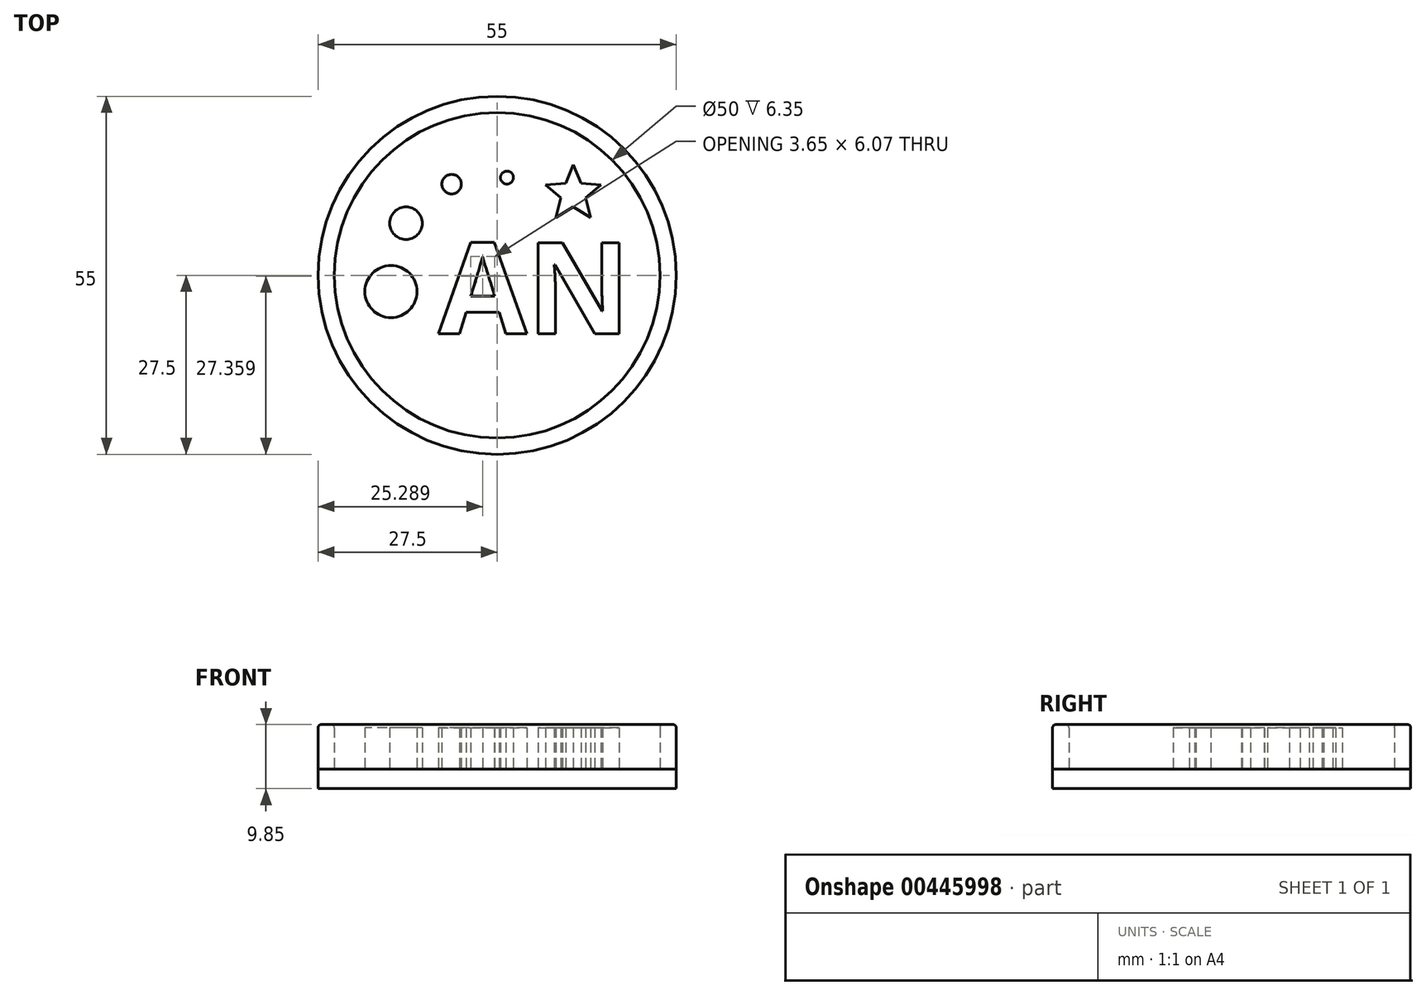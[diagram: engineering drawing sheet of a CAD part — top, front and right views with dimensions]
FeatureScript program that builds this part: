
annotation { "Feature Type Name" : "Feature", "Feature Type Description" : "" }
export const myFeature = defineFeature(function(context is Context, id is Id, definition is map)
    precondition{}
    {
        {
            var Q0;
            Q0=qCreatedBy(makeId("Top.planeOp"),FACE);
            var sketch = newSketch(context, id + "F0", { "sketchPlane" : qUnion([Q0])});
            skCircle(sketch, "E0", {"center": v(0, 0) * mm, "radius": 27.5 * mm});
            skText(sketch, "E1", { "text": "AN", "fontName": "OpenSans-Bold.ttf"});
            skPoint(sketch, "E2", {"position": v(-16.3, -2.5) * mm});
            skPoint(sketch, "E3.1.0", {"position": v(-14, 8) * mm});
            skPoint(sketch, "E3.2.0", {"position": v(-7, 14) * mm});
            skPoint(sketch, "E3.3.0", {"position": v(1.5, 15) * mm});
            skCircle(sketch, "E4", {"center": v(-16.3, -2.5) * mm, "radius": 4 * mm});
            skCircle(sketch, "E5", {"center": v(-14, 8) * mm, "radius": 2.5 * mm});
            skCircle(sketch, "E6", {"center": v(-7, 14) * mm, "radius": 1.5 * mm});
            skPoint(sketch, "E7", {"position": v(11.69, 17) * mm});
            skPoint(sketch, "E8.1.0", {"position": v(7.4, 13.9) * mm});
            skPoint(sketch, "E8.2.0", {"position": v(9.04, 8.86) * mm});
            skPoint(sketch, "E8.3.0", {"position": v(14.33, 8.86) * mm});
            skPoint(sketch, "E8.4.0", {"position": v(15.96, 13.9) * mm});
            skPoint(sketch, "E8.center", {"position": v(11.69, 12.5) * mm});
            skPoint(sketch, "E9", {"position": v(11.69, 10.5) * mm});
            skPoint(sketch, "E10.1.0", {"position": v(13.59, 11.88) * mm});
            skPoint(sketch, "E10.2.0", {"position": v(12.86, 14.12) * mm});
            skPoint(sketch, "E10.3.0", {"position": v(10.5, 14.12) * mm});
            skPoint(sketch, "E10.4.0", {"position": v(9.78, 11.88) * mm});
            skLineSegment(sketch, "E11", {"start": v(11.69, 17) * mm, "end": v(10.5, 14.12) * mm});
            skLineSegment(sketch, "E12", {"start": v(10.5, 14.12) * mm, "end": v(7.4, 13.9) * mm});
            skLineSegment(sketch, "E13", {"start": v(7.4, 13.9) * mm, "end": v(9.78, 11.88) * mm});
            skLineSegment(sketch, "E14", {"start": v(9.78, 11.88) * mm, "end": v(9.04, 8.86) * mm});
            skLineSegment(sketch, "E15", {"start": v(9.04, 8.86) * mm, "end": v(11.69, 10.5) * mm});
            skLineSegment(sketch, "E16", {"start": v(11.69, 10.5) * mm, "end": v(14.33, 8.86) * mm});
            skLineSegment(sketch, "E17", {"start": v(14.33, 8.86) * mm, "end": v(13.59, 11.88) * mm});
            skLineSegment(sketch, "E18", {"start": v(13.59, 11.88) * mm, "end": v(15.96, 13.9) * mm});
            skLineSegment(sketch, "E19", {"start": v(15.96, 13.9) * mm, "end": v(12.86, 14.12) * mm});
            skLineSegment(sketch, "E20", {"start": v(12.86, 14.12) * mm, "end": v(11.69, 17) * mm});
            skCircle(sketch, "E21", {"center": v(1.5, 15) * mm, "radius": 1 * mm});
            skPoint(sketch, "E22", {"position": v(5.5, -1.94) * mm});
            skCircle(sketch, "E23", {"center": v(0, 0) * mm, "radius": 25 * mm});
            const initialGuessF0  = {"E1": [-0.009, -0.009, 1, 0, 0.01413]};
            skSetInitialGuess(sketch, initialGuessF0);
            skSolve(sketch);
        }
        {
            var Q0;
            Q0=makeQuery(id+"F0.imprint","IMPRINT",FACE,{"disambiguationData":[TD([[makeQuery(id+"F0.imprint","IMPRINT",EDGE,{"derivedFrom":sQuery(id+"F0.wireOp",EDGE,"E0")}),1.0]])]});
            var Q1;
            Q1=makeQuery(id+"F0.imprint","IMPRINT",FACE,{"disambiguationData":[TD([[makeQuery(id+"F0.imprint","IMPRINT",EDGE,{"derivedFrom":sQuery(id+"F0.wireOp",EDGE,"E4")}),1.0]])]});
            var Q2;
            Q2=makeQuery(id+"F0.imprint","IMPRINT",FACE,{"disambiguationData":[TD([[makeQuery(id+"F0.imprint","IMPRINT",EDGE,{"derivedFrom":sQuery(id+"F0.wireOp",EDGE,"E5")}),1.0]])]});
            var Q3;
            Q3=makeQuery(id+"F0.imprint","IMPRINT",FACE,{"disambiguationData":[TD([[makeQuery(id+"F0.imprint","IMPRINT",EDGE,{"derivedFrom":sQuery(id+"F0.wireOp",EDGE,"E1.sketch_text.stroke-0")}),-1.0]])]});
            var Q4;
            Q4=makeQuery(id+"F0.imprint","IMPRINT",FACE,{"disambiguationData":[TD([[makeQuery(id+"F0.imprint","IMPRINT",EDGE,{"derivedFrom":sQuery(id+"F0.wireOp",EDGE,"E1.sketch_text.stroke-12")}),-1.0]])]});
            var Q5;
            Q5=makeQuery(id+"F0.imprint","IMPRINT",FACE,{"disambiguationData":[TD([[makeQuery(id+"F0.imprint","IMPRINT",EDGE,{"derivedFrom":sQuery(id+"F0.wireOp",EDGE,"E11")}),1.0]])]});
            var Q6;
            Q6=makeQuery(id+"F0.imprint","IMPRINT",FACE,{"disambiguationData":[TD([[makeQuery(id+"F0.imprint","IMPRINT",EDGE,{"derivedFrom":sQuery(id+"F0.wireOp",EDGE,"E21")}),1.0]])]});
            var Q7;
            Q7=makeQuery(id+"F0.imprint","IMPRINT",FACE,{"disambiguationData":[TD([[makeQuery(id+"F0.imprint","IMPRINT",EDGE,{"derivedFrom":sQuery(id+"F0.wireOp",EDGE,"E6")}),1.0]])]});
            extrude(context, id + "F1", {"entities" : qUnion([Q0, Q1, Q2, Q3, Q4, Q5, Q6, Q7]), "depth" : 6.35 * mm});
        }
        {
            var Q0;
            Q0=qCreatedBy(makeId("Top.planeOp"),FACE);
            var sketch = newSketch(context, id + "F2", { "sketchPlane" : qUnion([Q0])});
            skCircle(sketch, "E24", {"center": v(0, 0) * mm, "radius": 27.5 * mm});
            skSolve(sketch);
        }
        {
            var Q0;
            Q0=makeQuery(id+"F2.imprint","IMPRINT",FACE,{"disambiguationData":[TD([[makeQuery(id+"F2.imprint","IMPRINT",EDGE,{"derivedFrom":sQuery(id+"F2.wireOp",EDGE,"E24")}),1.0]])]});
            extrude(context, id + "F3", {"entities" : qUnion([Q0]), "oppositeDirection" : true, "depth" : 3 * mm});
        }
        {
            var Q0;
            Q0=makeQuery(id+"F1.opExtrude","CAP_FACE",FACE,{"disambiguationData":[OSD([sQuery(id+"F0.wireOp",EDGE,"E0"),sQuery(id+"F0.wireOp",EDGE,"E23")])],"isStart":false});
            extrude(context, id + "F4", {"entities" : qUnion([Q0]), "operationType" : NewBodyOperationType.ADD, "depth" : .5 * mm});
        }
        {
            var Q0;
            Q0=makeQuery(id+"F4.opExtrude","CAP_FACE",FACE,{"disambiguationData":[OSD([sQuery(id+"F0.wireOp",EDGE,"E0"),sQuery(id+"F0.wireOp",EDGE,"E23")])],"isStart":false});
            fillet(context, id + "F5", {"entities" : qUnion([Q0]), "radius" : .5 * mm, "tangentPropagation" : true, "allowEdgeOverflow" : false});
        }
    });
